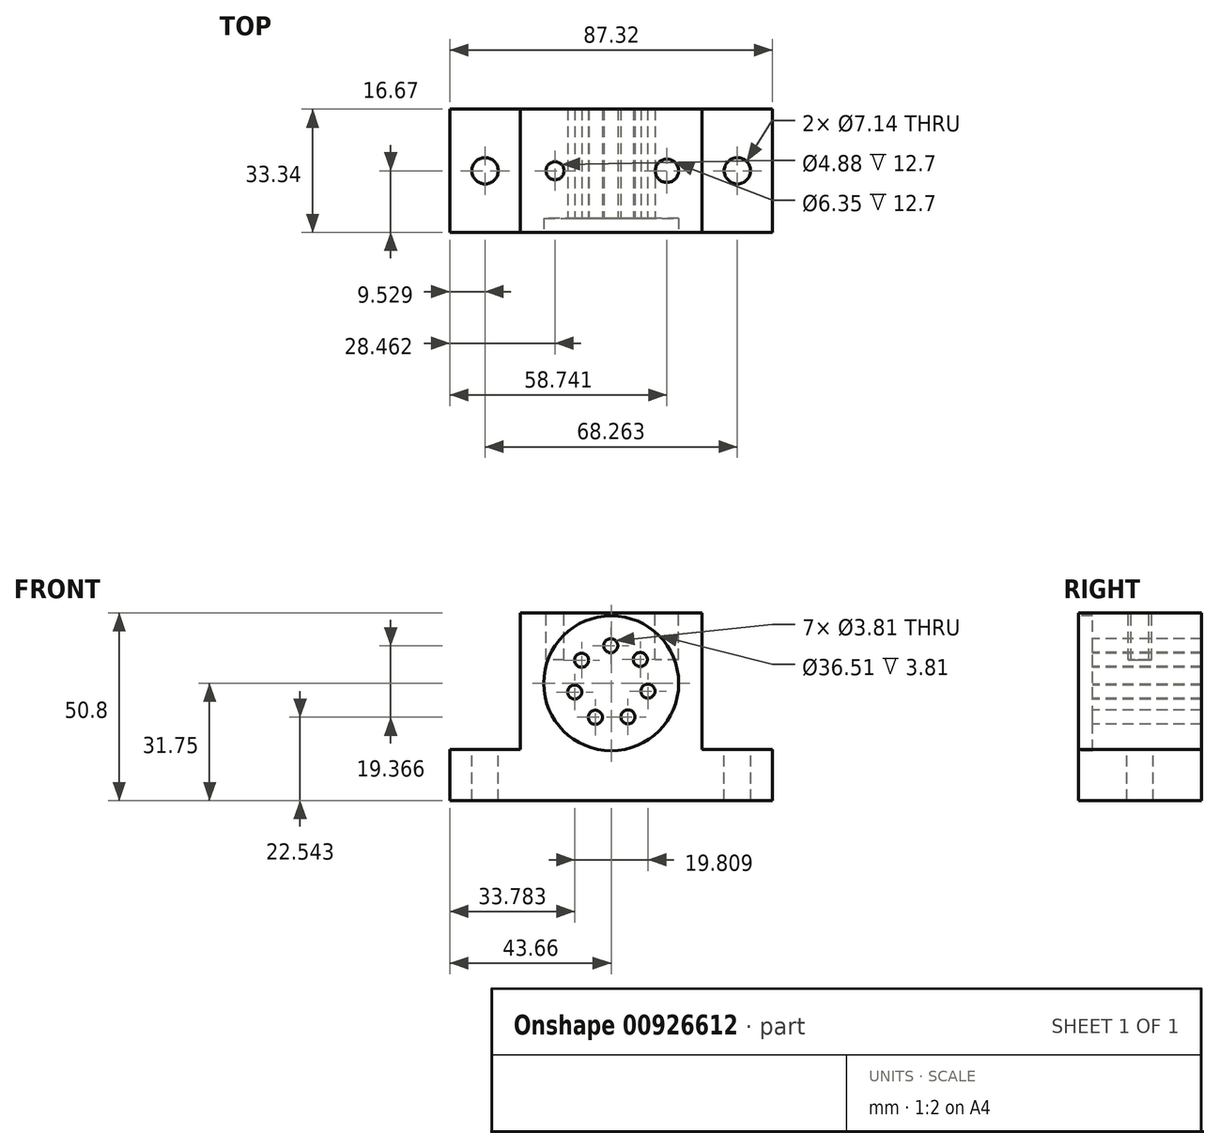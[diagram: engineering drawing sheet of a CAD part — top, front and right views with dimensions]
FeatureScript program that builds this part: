
annotation { "Feature Type Name" : "Feature", "Feature Type Description" : "" }
export const myFeature = defineFeature(function(context is Context, id is Id, definition is map)
    precondition{}
    {
        {
            var Q0;
            Q0=qCreatedBy(makeId("Front.planeOp"),FACE);
            var sketch = newSketch(context, id + "F0", { "sketchPlane" : qUnion([Q0])});
            skLineSegment(sketch, "E0", {"start": v(-43.66, 0) * mm, "end": v(-43.66, 13.83) * mm});
            skLineSegment(sketch, "E1", {"start": v(-43.66, 13.83) * mm, "end": v(-24.6, 13.83) * mm});
            skLineSegment(sketch, "E2", {"start": v(-24.6, 13.83) * mm, "end": v(-24.6, 50.8) * mm});
            skLineSegment(sketch, "E3", {"start": v(24.6, 50.8) * mm, "end": v(24.6, 13.83) * mm});
            skLineSegment(sketch, "E4", {"start": v(24.6, 13.83) * mm, "end": v(43.66, 13.83) * mm});
            skLineSegment(sketch, "E5", {"start": v(43.66, 13.83) * mm, "end": v(43.66, 0) * mm});
            skLineSegment(sketch, "E6", {"start": v(43.66, 0) * mm, "end": v(-43.66, 0) * mm});
            skLineSegment(sketch, "E7", {"start": v(-24.6, 50.8) * mm, "end": v(0, 50.8) * mm});
            skLineSegment(sketch, "E8", {"start": v(0, 50.8) * mm, "end": v(24.6, 50.8) * mm});
            skLineSegment(sketch, "E9", {"start": v(0, 0) * mm, "end": v(0, 50.8) * mm, "construction": true});
            skSolve(sketch);
        }
        {
            var Q0;
            Q0=makeQuery(id+"F0.imprint","IMPRINT",FACE,{"disambiguationData":[TD([[makeQuery(id+"F0.imprint","IMPRINT",EDGE,{"derivedFrom":sQuery(id+"F0.wireOp",EDGE,"E0")}),-1.0]])]});
            extrude(context, id + "F1", {"entities" : qUnion([Q0]), "endBound" : BoundingType.SYMMETRIC, "depth" : 33.34 * mm, "offsetDistance" : 25.4 * mm});
        }
        {
            var Q0;
            Q0=makeQuery(id+"F1.opExtrude","SWEPT_FACE",FACE,{"disambiguationData":[OSD([sQuery(id+"F0.wireOp",EDGE,"E1")])]});
            var sketch = newSketch(context, id + "F2", { "sketchPlane" : qUnion([Q0])});
            skCircle(sketch, "E10", {"center": v(-34.13, 0) * mm, "radius": 3.57 * mm});
            skCircle(sketch, "E11", {"center": v(34.13, 0) * mm, "radius": 3.57 * mm});
            skPoint(sketch, "E12", {"position": v(-24.6, 0) * mm});
            skLineSegment(sketch, "E13", {"start": v(-43.66, 0) * mm, "end": v(-34.13, 0) * mm, "construction": true});
            skLineSegment(sketch, "E14", {"start": v(-34.13, 0) * mm, "end": v(-24.6, 0) * mm, "construction": true});
            skLineSegment(sketch, "E15", {"start": v(34.13, 0) * mm, "end": v(24.6, 0) * mm, "construction": true});
            skLineSegment(sketch, "E16", {"start": v(34.13, 0) * mm, "end": v(43.66, 0) * mm, "construction": true});
            skSolve(sketch);
        }
        {
            var Q0;
            Q0 = qSketchRegion(id + "F2", true);
            extrude(context, id + "F3", {"entities" : qUnion([Q0]), "operationType" : NewBodyOperationType.REMOVE, "endBound" : BoundingType.THROUGH_ALL, "oppositeDirection" : true, "depth" : 25.4 * mm, "offsetDistance" : 25.4 * mm});
        }
        {
            var Q0;
            Q0=makeQuery(id+"F1.opExtrude","SWEPT_FACE",FACE,{"disambiguationData":[OSD([sQuery(id+"F0.wireOp",EDGE,"E7"),sQuery(id+"F0.wireOp",EDGE,"E8")])]});
            var sketch = newSketch(context, id + "F4", { "sketchPlane" : qUnion([Q0])});
            skCircle(sketch, "E17", {"center": v(15.08, 0) * mm, "radius": 3.18 * mm});
            skCircle(sketch, "E18", {"center": v(-15.2, 0) * mm, "radius": 2.44 * mm});
            skSolve(sketch);
        }
        {
            var Q0;
            Q0=makeQuery(id+"F4.imprint","IMPRINT",FACE,{"disambiguationData":[TD([[makeQuery(id+"F4.imprint","IMPRINT",EDGE,{"derivedFrom":sQuery(id+"F4.wireOp",EDGE,"E17")}),1.0]])]});
            var Q1;
            Q1=makeQuery(id+"F4.imprint","IMPRINT",FACE,{"disambiguationData":[TD([[makeQuery(id+"F4.imprint","IMPRINT",EDGE,{"derivedFrom":sQuery(id+"F4.wireOp",EDGE,"E18")}),1.0]])]});
            extrude(context, id + "F5", {"entities" : qUnion([Q0, Q1]), "operationType" : NewBodyOperationType.REMOVE, "oppositeDirection" : true, "depth" : 12.7 * mm, "offsetDistance" : 25.4 * mm});
        }
        {
            var Q0;
            Q0=makeQuery(id+"F1.opExtrude","CAP_FACE",FACE,{"disambiguationData":[OSD([sQuery(id+"F0.wireOp",EDGE,"E0"),sQuery(id+"F0.wireOp",EDGE,"E1"),sQuery(id+"F0.wireOp",EDGE,"E2"),sQuery(id+"F0.wireOp",EDGE,"E3"),sQuery(id+"F0.wireOp",EDGE,"E4"),sQuery(id+"F0.wireOp",EDGE,"E5"),sQuery(id+"F0.wireOp",EDGE,"E6"),sQuery(id+"F0.wireOp",EDGE,"E7"),sQuery(id+"F0.wireOp",EDGE,"E8")])],"isStart":false});
            var sketch = newSketch(context, id + "F6", { "sketchPlane" : qUnion([Q0])});
            skCircle(sketch, "E19", {"center": v(0, 31.75) * mm, "radius": 18.26 * mm});
            skLineSegment(sketch, "E20", {"start": v(18.26, 31.75) * mm, "end": v(24.6, 31.75) * mm, "construction": true});
            skLineSegment(sketch, "E21", {"start": v(0, 31.75) * mm, "end": v(18.26, 31.75) * mm, "construction": true});
            skLineSegment(sketch, "E22", {"start": v(0, 31.75) * mm, "end": v(-18.26, 31.75) * mm, "construction": true});
            skLineSegment(sketch, "E23", {"start": v(-18.26, 31.75) * mm, "end": v(-24.6, 31.75) * mm, "construction": true});
            skSolve(sketch);
        }
        {
            var Q0;
            Q0=makeQuery(id+"F6.imprint","IMPRINT",FACE,{"disambiguationData":[TD([[makeQuery(id+"F6.imprint","IMPRINT",EDGE,{"derivedFrom":sQuery(id+"F6.wireOp",EDGE,"E19")}),1.0]])]});
            extrude(context, id + "F7", {"entities" : qUnion([Q0]), "operationType" : NewBodyOperationType.REMOVE, "oppositeDirection" : true, "depth" : 3.8 * mm, "offsetDistance" : 25.4 * mm});
        }
        {
            var Q0;
            Q0=makeQuery(id+"F7.boolean.opBoolean","COPY",FACE,{"derivedFrom":makeQuery(id+"F7.opExtrude","CAP_FACE",FACE,{"disambiguationData":[OSD([sQuery(id+"F6.wireOp",EDGE,"E19")])],"isStart":false})});
            var sketch = newSketch(context, id + "F8", { "sketchPlane" : qUnion([Q0])});
            skCircle(sketch, "E24", {"center": v(-8.02, 37.99) * mm, "radius": 1.9 * mm});
            skCircle(sketch, "E25", {"center": v(0, 31.75) * mm, "radius": 10.16 * mm, "construction": true});
            skCircle(sketch, "E26.1.0", {"center": v(-9.88, 29.37) * mm, "radius": 1.9 * mm});
            skCircle(sketch, "E26.2.0", {"center": v(-4.3, 22.54) * mm, "radius": 1.9 * mm});
            skCircle(sketch, "E27.1.3.0", {"center": v(4.52, 22.65) * mm, "radius": 1.9 * mm});
            skCircle(sketch, "E27.1.4.0", {"center": v(9.93, 29.6) * mm, "radius": 1.9 * mm});
            skCircle(sketch, "E27.1.5.0", {"center": v(7.87, 38.18) * mm, "radius": 1.9 * mm});
            skCircle(sketch, "E27.1.6.0", {"center": v(-0.12, 41.9) * mm, "radius": 1.9 * mm});
            skSolve(sketch);
        }
        {
            var Q0;
            Q0=makeQuery(id+"F8.imprint","IMPRINT",FACE,{"disambiguationData":[TD([[makeQuery(id+"F8.imprint","IMPRINT",EDGE,{"derivedFrom":sQuery(id+"F8.wireOp",EDGE,"E24")}),1.0]])]});
            var Q1;
            Q1=makeQuery(id+"F8.imprint","IMPRINT",FACE,{"disambiguationData":[TD([[makeQuery(id+"F8.imprint","IMPRINT",EDGE,{"derivedFrom":sQuery(id+"F8.wireOp",EDGE,"E27.1.6.0")}),1.0]])]});
            var Q2;
            Q2=makeQuery(id+"F8.imprint","IMPRINT",FACE,{"disambiguationData":[TD([[makeQuery(id+"F8.imprint","IMPRINT",EDGE,{"derivedFrom":sQuery(id+"F8.wireOp",EDGE,"E27.1.5.0")}),1.0]])]});
            var Q3;
            Q3=makeQuery(id+"F8.imprint","IMPRINT",FACE,{"disambiguationData":[TD([[makeQuery(id+"F8.imprint","IMPRINT",EDGE,{"derivedFrom":sQuery(id+"F8.wireOp",EDGE,"E27.1.4.0")}),1.0]])]});
            var Q4;
            Q4=makeQuery(id+"F8.imprint","IMPRINT",FACE,{"disambiguationData":[TD([[makeQuery(id+"F8.imprint","IMPRINT",EDGE,{"derivedFrom":sQuery(id+"F8.wireOp",EDGE,"E27.1.3.0")}),1.0]])]});
            var Q5;
            Q5=makeQuery(id+"F8.imprint","IMPRINT",FACE,{"disambiguationData":[TD([[makeQuery(id+"F8.imprint","IMPRINT",EDGE,{"derivedFrom":sQuery(id+"F8.wireOp",EDGE,"E26.2.0")}),1.0]])]});
            var Q6;
            Q6=makeQuery(id+"F8.imprint","IMPRINT",FACE,{"disambiguationData":[TD([[makeQuery(id+"F8.imprint","IMPRINT",EDGE,{"derivedFrom":sQuery(id+"F8.wireOp",EDGE,"E26.1.0")}),1.0]])]});
            extrude(context, id + "F9", {"entities" : qUnion([Q0, Q1, Q2, Q3, Q4, Q5, Q6]), "operationType" : NewBodyOperationType.REMOVE, "endBound" : BoundingType.THROUGH_ALL, "oppositeDirection" : true, "depth" : 25.4 * mm, "offsetDistance" : 25.4 * mm});
        }
    });
